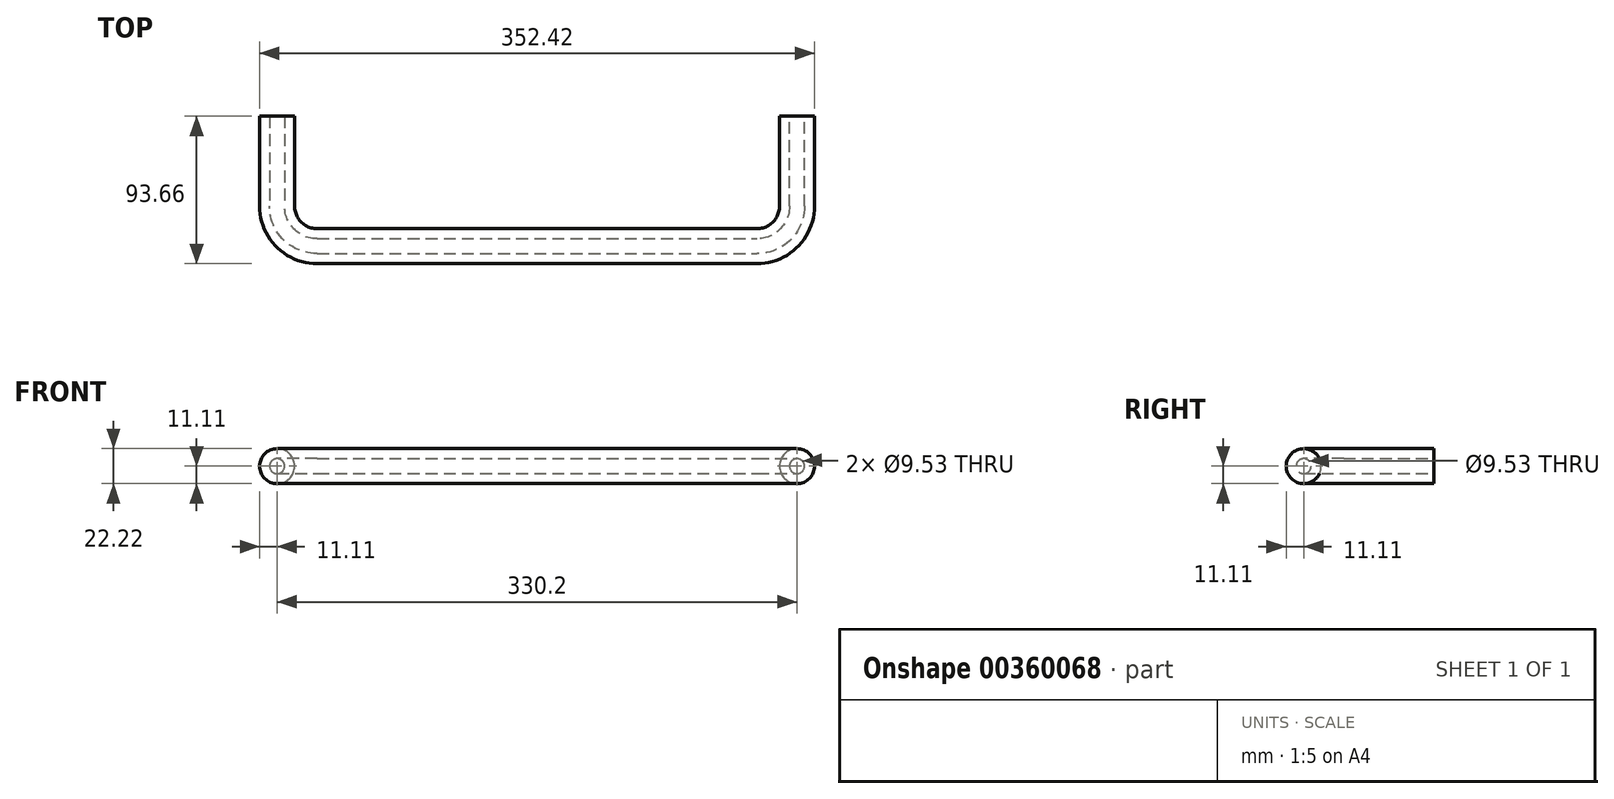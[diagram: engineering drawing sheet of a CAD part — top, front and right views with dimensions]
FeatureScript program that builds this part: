
annotation { "Feature Type Name" : "Feature", "Feature Type Description" : "" }
export const myFeature = defineFeature(function(context is Context, id is Id, definition is map)
    precondition{}
    {
        {
            var Q0;
            Q0=qCreatedBy(makeId("Top.planeOp"),FACE);
            var sketch = newSketch(context, id + "F0", { "sketchPlane" : qUnion([Q0])});
            skLineSegment(sketch, "E0", {"start": v(0, 0) * mm, "end": v(0, -57.15) * mm});
            skArc(sketch, "E1", {"start": v(0, -57.15) * mm, "mid": v(7.44, -75.11) * mm, "end": v(25.4, -82.55) * mm});
            skLineSegment(sketch, "E2", {"start": v(25.4, -82.55) * mm, "end": v(304.8, -82.55) * mm});
            skArc(sketch, "E3", {"start": v(304.8, -82.55) * mm, "mid": v(322.76, -75.11) * mm, "end": v(330.2, -57.15) * mm});
            skLineSegment(sketch, "E4", {"start": v(330.2, -57.15) * mm, "end": v(330.2, 0) * mm});
            skSolve(sketch);
        }
        {
            var Q0;
            Q0=qCreatedBy(makeId("Front.planeOp"),FACE);
            var sketch = newSketch(context, id + "F1", { "sketchPlane" : qUnion([Q0])});
            skCircle(sketch, "E5", {"center": v(0, 0) * mm, "radius": 11.11 * mm});
            skCircle(sketch, "E6", {"center": v(0, 0) * mm, "radius": 4.76 * mm});
            skSolve(sketch);
        }
        {
            var Q0;
            Q0 = qSketchRegion(id + "F1", true);
            var Q1;
            Q1 = qConstructionFilter(qBodyType(qCreatedBy(id + "F1" ,EDGE), BodyType.WIRE), ConstructionObject.NO);
            var Q2;
            Q2=sQuery(id+"F0.wireOp",EDGE,"E0");
            var Q3;
            Q3=sQuery(id+"F0.wireOp",EDGE,"E1");
            var Q4;
            Q4=sQuery(id+"F0.wireOp",EDGE,"E2");
            var Q5;
            Q5=sQuery(id+"F0.wireOp",EDGE,"E3");
            var Q6;
            Q6=sQuery(id+"F0.wireOp",EDGE,"E4");
            sweep(context, id + "F2", {"profiles" : qUnion([Q0]), "surfaceProfiles" : qUnion([Q1]), "path" : qUnion([Q2, Q3, Q4, Q5, Q6])});
        }
    });
